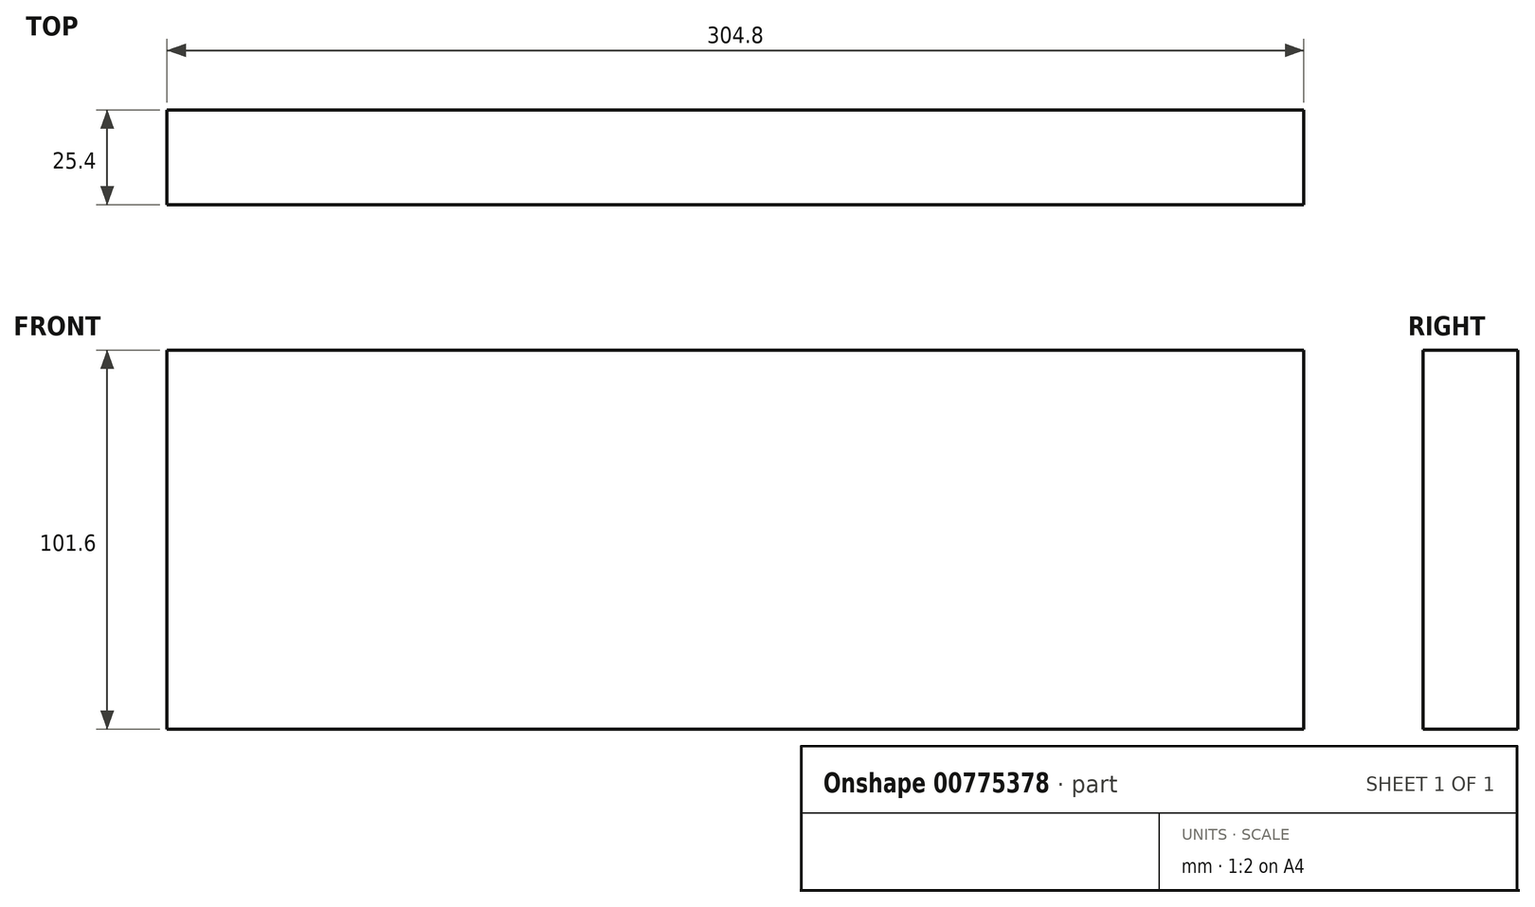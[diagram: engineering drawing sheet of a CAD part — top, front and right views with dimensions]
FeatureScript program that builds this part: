
annotation { "Feature Type Name" : "Feature", "Feature Type Description" : "" }
export const myFeature = defineFeature(function(context is Context, id is Id, definition is map)
    precondition{}
    {
        {
            var Q0;
            Q0=qCreatedBy(makeId("Front.planeOp"),FACE);
            var sketch = newSketch(context, id + "F0", { "sketchPlane" : qUnion([Q0])});
            skLineSegment(sketch, "E0.bottom", {"start": v(-152.4, 50.8) * mm, "end": v(152.4, 50.8) * mm});
            skLineSegment(sketch, "E0.top", {"start": v(-152.4, -50.8) * mm, "end": v(152.4, -50.8) * mm});
            skLineSegment(sketch, "E0.left", {"start": v(-152.4, 50.8) * mm, "end": v(-152.4, -50.8) * mm});
            skLineSegment(sketch, "E0.right", {"start": v(152.4, 50.8) * mm, "end": v(152.4, -50.8) * mm});
            skPoint(sketch, "E0.middle", {"position": v(0, 0) * mm});
            skSolve(sketch);
        }
        {
            var Q0;
            Q0 = qSketchRegion(id + "F0", true);
            extrude(context, id + "F1", {"entities" : qUnion([Q0]), "endBound" : BoundingType.SYMMETRIC, "depth" : 25.4 * mm, "offsetDistance" : 25.4 * mm});
        }
    });
